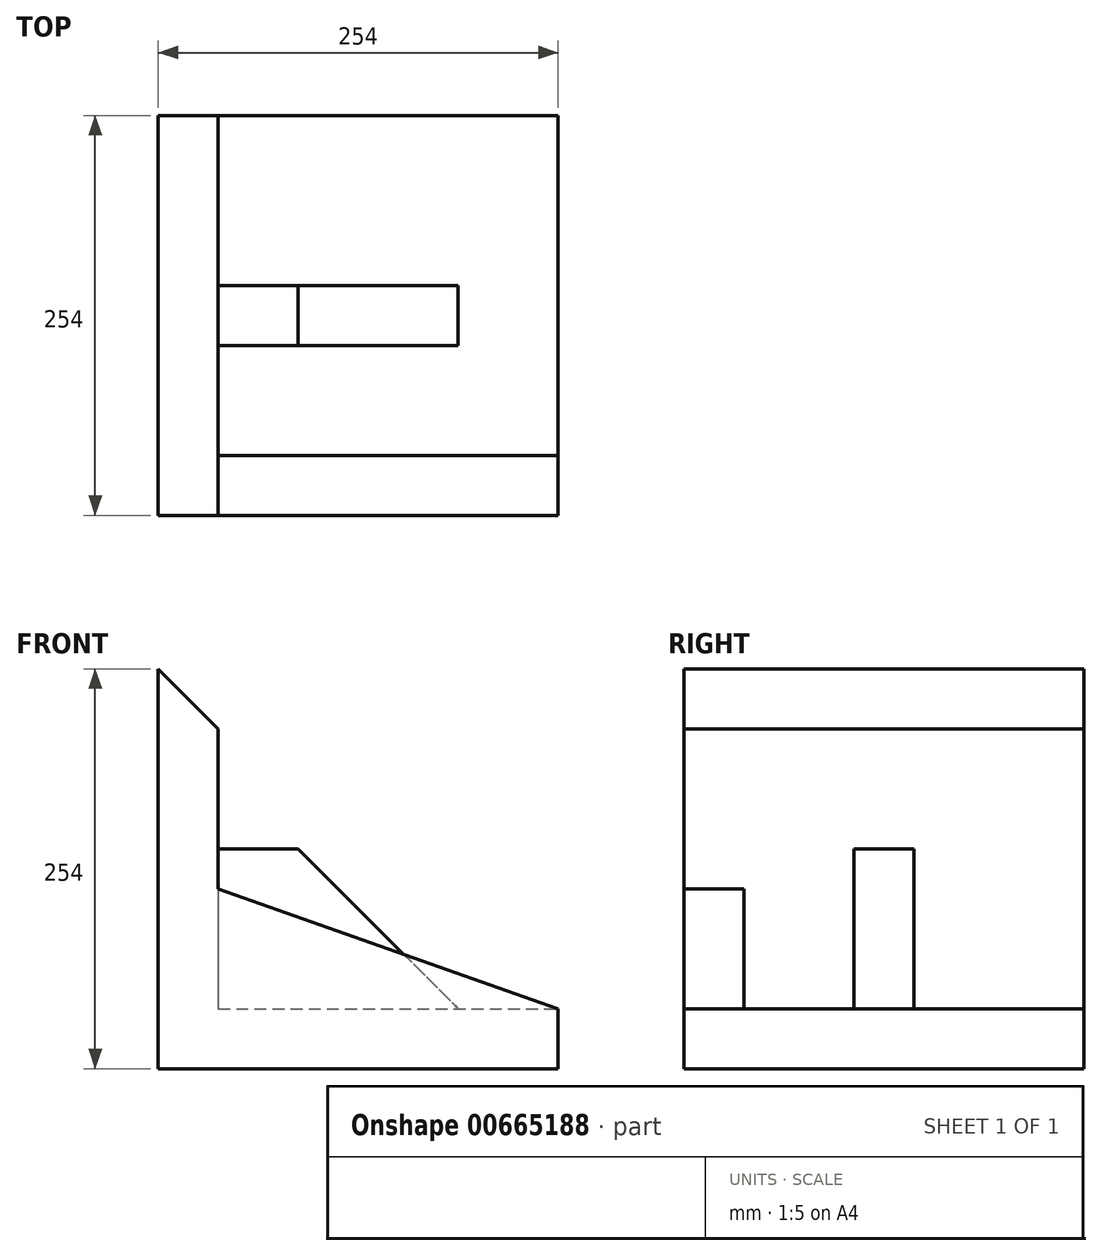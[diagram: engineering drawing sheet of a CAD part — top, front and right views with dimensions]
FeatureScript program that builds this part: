
annotation { "Feature Type Name" : "Feature", "Feature Type Description" : "" }
export const myFeature = defineFeature(function(context is Context, id is Id, definition is map)
    precondition{}
    {
        {
            var Q0;
            Q0=qCreatedBy(makeId("Front.planeOp"),FACE);
            var sketch = newSketch(context, id + "F0", { "sketchPlane" : qUnion([Q0])});
            skLineSegment(sketch, "E0", {"start": v(0, 0) * mm, "end": v(254, 0) * mm});
            skLineSegment(sketch, "E1", {"start": v(0, 0) * mm, "end": v(0, 254) * mm});
            skLineSegment(sketch, "E2", {"start": v(38.1, 215.9) * mm, "end": v(38.1, 139.7) * mm});
            skLineSegment(sketch, "E3", {"start": v(38.1, 139.7) * mm, "end": v(88.9, 139.7) * mm});
            skLineSegment(sketch, "E4", {"start": v(38.1, 215.9) * mm, "end": v(0, 254) * mm});
            skLineSegment(sketch, "E5", {"start": v(38.1, 139.7) * mm, "end": v(38.1, 38.1) * mm});
            skLineSegment(sketch, "E6", {"start": v(88.9, 139.7) * mm, "end": v(190.5, 38.1) * mm});
            skLineSegment(sketch, "E7", {"start": v(38.1, 38.1) * mm, "end": v(190.5, 38.1) * mm});
            skLineSegment(sketch, "E8", {"start": v(190.5, 38.1) * mm, "end": v(254, 38.1) * mm});
            skLineSegment(sketch, "E9", {"start": v(254, 38.1) * mm, "end": v(254, 0) * mm});
            skSolve(sketch);
        }
        {
            var Q0;
            Q0=makeQuery(id+"F0.imprint","IMPRINT",FACE,{"disambiguationData":[TD([[makeQuery(id+"F0.imprint","IMPRINT",EDGE,{"derivedFrom":sQuery(id+"F0.wireOp",EDGE,"E0")}),1.0]])]});
            extrude(context, id + "F1", {"entities" : qUnion([Q0]), "endBound" : BoundingType.SYMMETRIC, "depth" : 254 * mm, "offsetDistance" : 25.4 * mm});
        }
        {
            var Q0;
            Q0=makeQuery(id+"F0.imprint","IMPRINT",FACE,{"disambiguationData":[TD([[makeQuery(id+"F0.imprint","IMPRINT",EDGE,{"derivedFrom":sQuery(id+"F0.wireOp",EDGE,"E3")}),-1.0]])]});
            extrude(context, id + "F2", {"entities" : qUnion([Q0]), "operationType" : NewBodyOperationType.ADD, "endBound" : BoundingType.SYMMETRIC, "depth" : 38.1 * mm, "offsetDistance" : 25.4 * mm});
        }
        {
            var Q0;
            Q0=makeQuery(id+"F1.opExtrude","CAP_FACE",FACE,{"disambiguationData":[OSD([sQuery(id+"F0.wireOp",EDGE,"E0"),sQuery(id+"F0.wireOp",EDGE,"E1"),sQuery(id+"F0.wireOp",EDGE,"E2"),sQuery(id+"F0.wireOp",EDGE,"E4"),sQuery(id+"F0.wireOp",EDGE,"E5"),sQuery(id+"F0.wireOp",EDGE,"E7"),sQuery(id+"F0.wireOp",EDGE,"E8"),sQuery(id+"F0.wireOp",EDGE,"E9")])],"isStart":false});
            var sketch = newSketch(context, id + "F3", { "sketchPlane" : qUnion([Q0])});
            skLineSegment(sketch, "E10", {"start": v(38.1, 114.3) * mm, "end": v(254, 38.1) * mm});
            skSolve(sketch);
        }
        {
            var Q0;
            {var subQ0=sQuery(id+"F3.wireOp",EDGE,"E10");Q0=makeQuery(id+"F3.imprint","IMPRINT",FACE,{"disambiguationData":[TD([[makeQuery(id+"F3.imprint","IMPRINT",EDGE,{"derivedFrom":subQ0}),-1.0]])]});}
            extrude(context, id + "F4", {"entities" : qUnion([Q0]), "operationType" : NewBodyOperationType.ADD, "oppositeDirection" : true, "depth" : 38.1 * mm, "offsetDistance" : 25.4 * mm});
        }
    });
